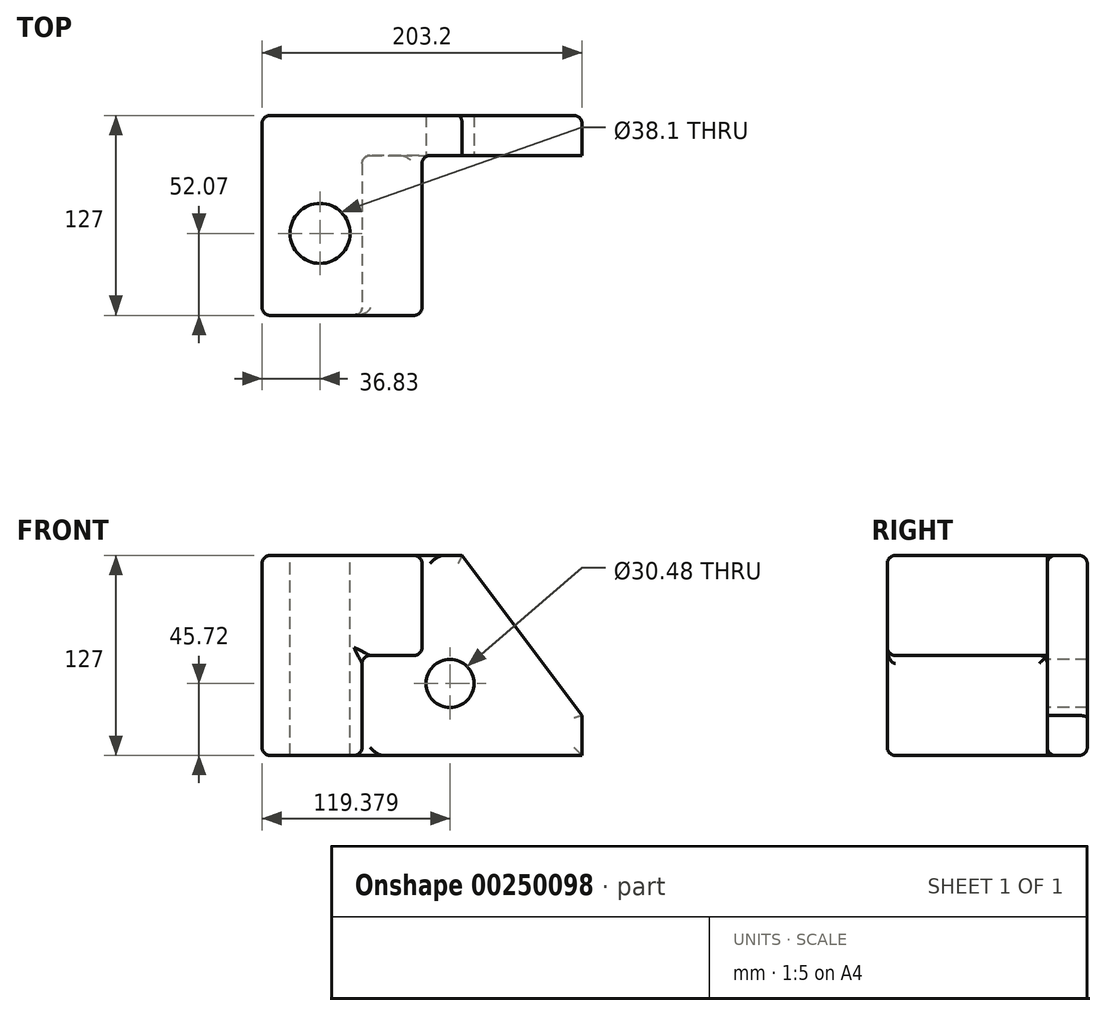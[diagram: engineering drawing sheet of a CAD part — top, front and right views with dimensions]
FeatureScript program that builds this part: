
annotation { "Feature Type Name" : "Feature", "Feature Type Description" : "" }
export const myFeature = defineFeature(function(context is Context, id is Id, definition is map)
    precondition{}
    {
        {
            var Q0;
            Q0=qCreatedBy(makeId("Front.planeOp"),FACE);
            var sketch = newSketch(context, id + "F0", { "sketchPlane" : qUnion([Q0])});
            skLineSegment(sketch, "E0.bottom", {"start": v(101.6, 63.5) * mm, "end": v(-101.6, 63.5) * mm});
            skLineSegment(sketch, "E0.top", {"start": v(101.6, -63.5) * mm, "end": v(-101.6, -63.5) * mm});
            skLineSegment(sketch, "E0.left", {"start": v(101.6, 63.5) * mm, "end": v(101.6, -63.5) * mm});
            skLineSegment(sketch, "E0.right", {"start": v(-101.6, 63.5) * mm, "end": v(-101.6, -63.5) * mm});
            skPoint(sketch, "E0.middle", {"position": v(0, 0) * mm});
            skSolve(sketch);
        }
        {
            var Q0;
            Q0 = qSketchRegion(id + "F0", true);
            extrude(context, id + "F1", {"entities" : qUnion([Q0]), "depth" : 127 * mm});
        }
        {
            var Q0;
            Q0=makeQuery(id+"F1.opExtrude","CAP_FACE",FACE,{"disambiguationData":[OSD([sQuery(id+"F0.wireOp",EDGE,"E0.bottom"),sQuery(id+"F0.wireOp",EDGE,"E0.top"),sQuery(id+"F0.wireOp",EDGE,"E0.left"),sQuery(id+"F0.wireOp",EDGE,"E0.right")])],"isStart":false});
            var sketch = newSketch(context, id + "F2", { "sketchPlane" : qUnion([Q0])});
            skLineSegment(sketch, "E1", {"start": v(-101.6, -63.5) * mm, "end": v(-101.6, 63.5) * mm});
            skLineSegment(sketch, "E2", {"start": v(-101.6, 63.5) * mm, "end": v(0, 63.5) * mm});
            skLineSegment(sketch, "E3", {"start": v(-101.6, -63.5) * mm, "end": v(-38.1, -63.5) * mm});
            skLineSegment(sketch, "E4", {"start": v(-38.1, -63.5) * mm, "end": v(-38.1, 0) * mm});
            skLineSegment(sketch, "E5", {"start": v(-38.1, 0) * mm, "end": v(0, 0) * mm});
            skLineSegment(sketch, "E6", {"start": v(0, 0) * mm, "end": v(0, 63.5) * mm});
            skSolve(sketch);
        }
        {
            var Q0;
            {var subQ3=sQuery(id+"F2.wireOp",EDGE,"E4");Q0=makeQuery(id+"F2.imprint","IMPRINT",FACE,{"disambiguationData":[TD([[makeQuery(id+"F2.imprint","IMPRINT",EDGE,{"derivedFrom":subQ3}),-1.0]])]});}
            extrude(context, id + "F3", {"entities" : qUnion([Q0]), "operationType" : NewBodyOperationType.REMOVE, "oppositeDirection" : true, "depth" : 101.6 * mm});
        }
        {
            var Q0;
            Q0=makeQuery(id+"F1.opExtrude","SWEPT_EDGE",EDGE,{"disambiguationData":[OSD([sQuery(id+"F0.wireOp",EDGE,"E0.bottom"),sQuery(id+"F0.wireOp",EDGE,"E0.left")])]});
            chamfer(context, id + "F4", {"entities" : qUnion([Q0]), "chamferType" : ChamferType.TWO_OFFSETS, "width1" : 76.2 * mm, "oppositeDirection" : false, "width2" : 101.6 * mm, "tangentPropagation" : true});
        }
        {
            var Q0;
            Q0=makeQuery(id+"F1.opExtrude","CAP_FACE",FACE,{"disambiguationData":[OSD([sQuery(id+"F0.wireOp",EDGE,"E0.bottom"),sQuery(id+"F0.wireOp",EDGE,"E0.top"),sQuery(id+"F0.wireOp",EDGE,"E0.left"),sQuery(id+"F0.wireOp",EDGE,"E0.right")])],"isStart":false});
            var Q1;
            Q1=makeQuery(id+"F3.boolean.opBoolean","COPY",FACE,{"derivedFrom":makeQuery(id+"F3.opExtrude","SWEPT_FACE",FACE,{"disambiguationData":[OSD([sQuery(id+"F2.wireOp",EDGE,"E6")])]})});
            fillet(context, id + "F5", {"entities" : qUnion([Q0, Q1]), "radius" : 5.08 * mm, "tangentPropagation" : true, "allowEdgeOverflow" : false});
        }
        {
            var Q0;
            Q0=makeQuery(id+"F3.boolean.opBoolean","COPY",FACE,{"derivedFrom":makeQuery(id+"F3.opExtrude","SWEPT_FACE",FACE,{"disambiguationData":[OSD([sQuery(id+"F2.wireOp",EDGE,"E4")])]})});
            var Q1;
            Q1=makeQuery(id+"F1.opExtrude","CAP_FACE",FACE,{"disambiguationData":[OSD([sQuery(id+"F0.wireOp",EDGE,"E0.bottom"),sQuery(id+"F0.wireOp",EDGE,"E0.top"),sQuery(id+"F0.wireOp",EDGE,"E0.left"),sQuery(id+"F0.wireOp",EDGE,"E0.right")])],"isStart":false});
            fillet(context, id + "F6", {"entities" : qUnion([Q0, Q1]), "radius" : 5.08 * mm, "tangentPropagation" : true, "allowEdgeOverflow" : false});
        }
        {
            var Q0;
            Q0=makeQuery(id+"F1.opExtrude","SWEPT_FACE",FACE,{"disambiguationData":[OSD([sQuery(id+"F0.wireOp",EDGE,"E0.right")])]});
            var Q1;
            Q1=makeQuery(id+"F1.opExtrude","CAP_FACE",FACE,{"disambiguationData":[OSD([sQuery(id+"F0.wireOp",EDGE,"E0.bottom"),sQuery(id+"F0.wireOp",EDGE,"E0.top"),sQuery(id+"F0.wireOp",EDGE,"E0.left"),sQuery(id+"F0.wireOp",EDGE,"E0.right")])],"isStart":true});
            fillet(context, id + "F7", {"entities" : qUnion([Q0, Q1]), "radius" : 5.08 * mm, "tangentPropagation" : true, "allowEdgeOverflow" : false});
        }
        {
            var Q0;
            Q0=makeQuery(id+"F3.boolean.opBoolean","COPY",FACE,{"derivedFrom":makeQuery(id+"F3.opExtrude","CAP_FACE",FACE,{"disambiguationData":[OSD([sQuery(id+"F0.wireOp",EDGE,"E0.bottom"),sQuery(id+"F0.wireOp",EDGE,"E0.top"),sQuery(id+"F0.wireOp",EDGE,"E0.left"),sQuery(id+"F2.wireOp",EDGE,"E4"),sQuery(id+"F2.wireOp",EDGE,"E5"),sQuery(id+"F2.wireOp",EDGE,"E6")])],"isStart":false})});
            var sketch = newSketch(context, id + "F8", { "sketchPlane" : qUnion([Q0])});
            skCircle(sketch, "E7", {"center": v(17.78, -17.78) * mm, "radius": 15.24 * mm});
            skSolve(sketch);
        }
        {
            var Q0;
            Q0 = qSketchRegion(id + "F8", true);
            var Q1;
            Q1=makeQuery(id+"F1.opExtrude","CAP_FACE",FACE,{"disambiguationData":[OSD([sQuery(id+"F0.wireOp",EDGE,"E0.bottom"),sQuery(id+"F0.wireOp",EDGE,"E0.top"),sQuery(id+"F0.wireOp",EDGE,"E0.left"),sQuery(id+"F0.wireOp",EDGE,"E0.right")])],"isStart":true});
            extrude(context, id + "F9", {"entities" : qUnion([Q0]), "operationType" : NewBodyOperationType.REMOVE, "endBound" : BoundingType.UP_TO_SURFACE, "oppositeDirection" : true, "endBoundEntityFace" : qUnion([Q1]), "depth" : 25.4 * mm});
        }
        {
            var Q0;
            Q0=makeQuery(id+"F1.opExtrude","SWEPT_FACE",FACE,{"disambiguationData":[OSD([sQuery(id+"F0.wireOp",EDGE,"E0.bottom")])]});
            var sketch = newSketch(context, id + "F10", { "sketchPlane" : qUnion([Q0])});
            skCircle(sketch, "E8", {"center": v(-64.77, -74.93) * mm, "radius": 19.05 * mm});
            skSolve(sketch);
        }
        {
            var Q0;
            Q0=makeQuery(id+"F10.imprint","IMPRINT",FACE,{"disambiguationData":[TD([[makeQuery(id+"F10.imprint","IMPRINT",EDGE,{"derivedFrom":sQuery(id+"F10.wireOp",EDGE,"E8")}),1.0]])]});
            var Q1;
            Q1=makeQuery(id+"F1.opExtrude","SWEPT_FACE",FACE,{"disambiguationData":[OSD([sQuery(id+"F0.wireOp",EDGE,"E0.top")])]});
            extrude(context, id + "F11", {"entities" : qUnion([Q0]), "operationType" : NewBodyOperationType.REMOVE, "endBound" : BoundingType.UP_TO_SURFACE, "oppositeDirection" : true, "endBoundEntityFace" : qUnion([Q1]), "depth" : 25.4 * mm});
        }
    });
